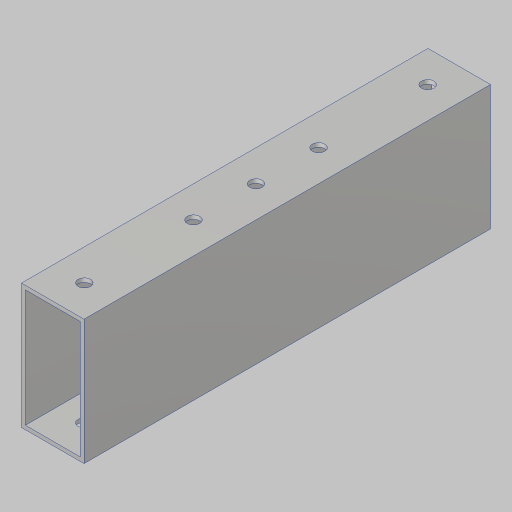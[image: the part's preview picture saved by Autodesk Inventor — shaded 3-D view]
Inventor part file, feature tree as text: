
AUTODESK INVENTOR PART (.ipt)
format: ipt  version: 2023.5 (Build 275446000, 446)  size: 228,352 bytes
history: native  units: in
note: dims shown in document units (in); Inventor stores cm internally (conversion verified against a paired STEP export)
features: hole x2, sketch x2, extrude x1
ambient origin geometry x8: Origin, YZ Plane, XZ Plane, XY Plane, X Axis, Y Axis, Z Axis, Center Point
bodies: Solid1 (feature_tree)
feature tree (5):
  extrude  "Extrusion1"  Depth=1.0in
  hole  "Hole3"  [1 undecoded]
  hole  "Hole4"  [1 undecoded]
  sketch  "Sketch5"  dims[d4=0.0in d28=1.0in]
  sketch  "Sketch6"  dims[d29=1.0in d30=0.201in d31=0.75in d32=0.385in d33=0.25in d34=0.5635in d35=1.0in d36=0.8108in d37=5.49in d38=0.201in d39=0.75in d40=0.385in d41=0.25in d42=0.5635in d43=1.0in d44=0.8108in]
note: 2 required parameter values undecoded (feature->parameter linkage not recoverable at this tier; creation-order binding heuristic only, values carry confidence <= 0.55)
